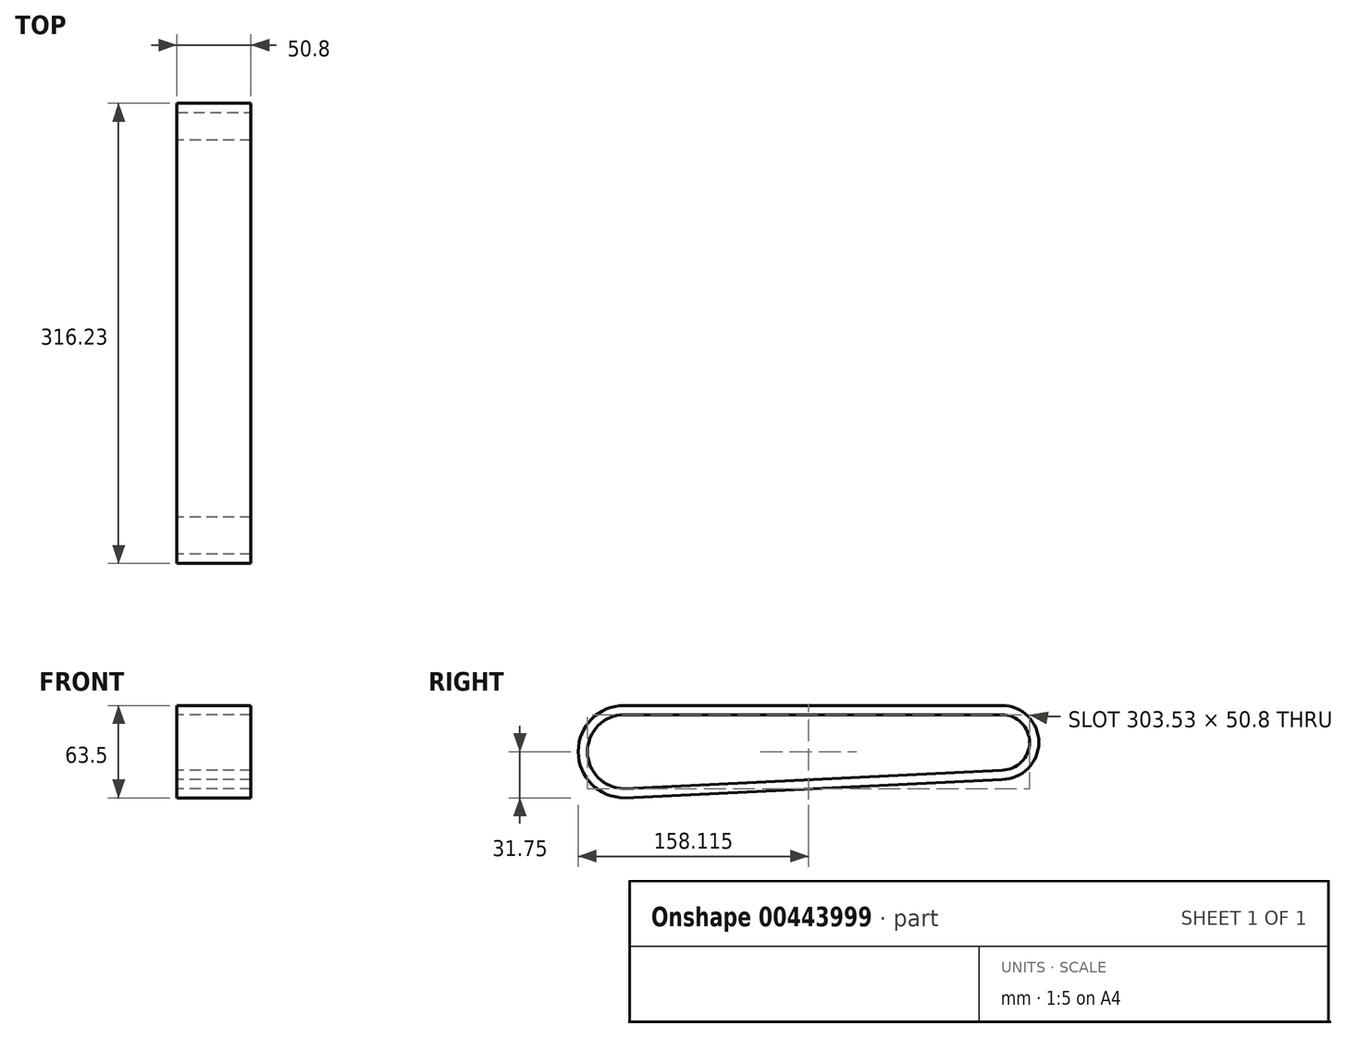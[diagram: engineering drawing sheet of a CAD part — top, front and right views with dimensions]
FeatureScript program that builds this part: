
annotation { "Feature Type Name" : "Feature", "Feature Type Description" : "" }
export const myFeature = defineFeature(function(context is Context, id is Id, definition is map)
    precondition{}
    {
        {
            var Q0;
            Q0=qCreatedBy(makeId("Front.planeOp"),FACE);
            var sketch = newSketch(context, id + "F0", { "sketchPlane" : qUnion([Q0])});
            skLineSegment(sketch, "E0.bottom", {"start": v(0, 0) * mm, "end": v(-50.8, 0) * mm});
            skLineSegment(sketch, "E0.top", {"start": v(0, 6.35) * mm, "end": v(-50.8, 6.35) * mm});
            skLineSegment(sketch, "E0.left", {"start": v(0, 0) * mm, "end": v(0, 6.35) * mm});
            skLineSegment(sketch, "E0.right", {"start": v(-50.8, 0) * mm, "end": v(-50.8, 6.35) * mm});
            skSolve(sketch);
        }
        {
            var Q0;
            Q0=makeQuery(id+"F0.imprint","IMPRINT",FACE,{"disambiguationData":[TD([[makeQuery(id+"F0.imprint","IMPRINT",EDGE,{"derivedFrom":sQuery(id+"F0.wireOp",EDGE,"E0.bottom")}),-1.0]])]});
            extrude(context, id + "F1", {"entities" : qUnion([Q0]), "depth" : 259.08 * mm});
        }
        {
            var Q0;
            Q0=makeQuery(id+"F1.opExtrude","CAP_FACE",FACE,{"disambiguationData":[OSD([sQuery(id+"F0.wireOp",EDGE,"E0.bottom"),sQuery(id+"F0.wireOp",EDGE,"E0.top"),sQuery(id+"F0.wireOp",EDGE,"E0.left"),sQuery(id+"F0.wireOp",EDGE,"E0.right")])],"isStart":false});
            var sketch = newSketch(context, id + "F2", { "sketchPlane" : qUnion([Q0])});
            skLineSegment(sketch, "E1.bottom", {"start": v(0, 0) * mm, "end": v(-50.8, 0) * mm});
            skLineSegment(sketch, "E1.top", {"start": v(0, 6.35) * mm, "end": v(-50.8, 6.35) * mm});
            skLineSegment(sketch, "E1.left", {"start": v(0, 0) * mm, "end": v(0, 6.35) * mm});
            skLineSegment(sketch, "E1.right", {"start": v(-50.8, 0) * mm, "end": v(-50.8, 6.35) * mm});
            skLineSegment(sketch, "E2", {"start": v(0, -25.4) * mm, "end": v(0, 0) * mm});
            skLineSegment(sketch, "E3", {"start": v(0, -25.4) * mm, "end": v(-50.8, -25.4) * mm});
            skSolve(sketch);
        }
        {
            var Q0;
            Q0=makeQuery(id+"F2.imprint","IMPRINT",FACE,{"disambiguationData":[TD([[makeQuery(id+"F2.imprint","IMPRINT",EDGE,{"derivedFrom":sQuery(id+"F2.wireOp",EDGE,"E1.bottom")}),-1.0]])]});
            var Q1;
            Q1=sQuery(id+"F2.wireOp",EDGE,"E3");
            revolve(context, id + "F3", {"operationType" : NewBodyOperationType.ADD, "entities" : qUnion([Q0]), "axis" : qUnion([Q1]), "revolveType" : RevolveType.ONE_DIRECTION, "oppositeDirection" : true, "angle" : 180 * degree});
        }
        {
            var Q0;
            Q0=makeQuery(id+"F1.opExtrude","CAP_FACE",FACE,{"disambiguationData":[OSD([sQuery(id+"F0.wireOp",EDGE,"E0.bottom"),sQuery(id+"F0.wireOp",EDGE,"E0.top"),sQuery(id+"F0.wireOp",EDGE,"E0.left"),sQuery(id+"F0.wireOp",EDGE,"E0.right")])],"isStart":true});
            var sketch = newSketch(context, id + "F4", { "sketchPlane" : qUnion([Q0])});
            skLineSegment(sketch, "E4.bottom", {"start": v(0, 0) * mm, "end": v(50.8, 0) * mm});
            skLineSegment(sketch, "E4.top", {"start": v(0, 6.35) * mm, "end": v(50.8, 6.35) * mm});
            skLineSegment(sketch, "E4.left", {"start": v(0, 0) * mm, "end": v(0, 6.35) * mm});
            skLineSegment(sketch, "E4.right", {"start": v(50.8, 0) * mm, "end": v(50.8, 6.35) * mm});
            skLineSegment(sketch, "E5", {"start": v(0, 0) * mm, "end": v(0, -19.05) * mm});
            skLineSegment(sketch, "E6", {"start": v(0, -19.05) * mm, "end": v(63.5, -19.05) * mm});
            skSolve(sketch);
        }
        {
            var Q0;
            Q0=makeQuery(id+"F4.imprint","IMPRINT",FACE,{"disambiguationData":[TD([[makeQuery(id+"F4.imprint","IMPRINT",EDGE,{"derivedFrom":sQuery(id+"F4.wireOp",EDGE,"E4.bottom")}),1.0]])]});
            var Q1;
            Q1=sQuery(id+"F4.wireOp",EDGE,"E6");
            revolve(context, id + "F5", {"operationType" : NewBodyOperationType.ADD, "entities" : qUnion([Q0]), "axis" : qUnion([Q1]), "revolveType" : RevolveType.ONE_DIRECTION, "angle" : 180 * degree});
        }
        {
            var Q0;
            Q0=makeQuery(id+"F5.boolean.opBoolean","MERGE",FACE,{"derivedFrom":[makeQuery(id+"F3.boolean.opBoolean","MERGE",FACE,{"derivedFrom":[makeQuery(id+"F1.opExtrude","SWEPT_FACE",FACE,{"disambiguationData":[OSD([sQuery(id+"F0.wireOp",EDGE,"E0.right")])]}),makeQuery(id+"F3.opRevolve","SWEPT_FACE",FACE,{"disambiguationData":[OSD([sQuery(id+"F2.wireOp",EDGE,"E1.right")])]})]}),makeQuery(id+"F5.opRevolve","SWEPT_FACE",FACE,{"disambiguationData":[OSD([sQuery(id+"F4.wireOp",EDGE,"E4.right")])]})]});
            var sketch = newSketch(context, id + "F6", { "sketchPlane" : qUnion([Q0])});
            skLineSegment(sketch, "E7", {"start": v(0, -38.1) * mm, "end": v(259.08, -50.8) * mm});
            skLineSegment(sketch, "E8", {"start": v(259.08, -50.8) * mm, "end": v(259.08, -57.15) * mm});
            skLineSegment(sketch, "E9", {"start": v(259.08, -57.15) * mm, "end": v(0, -44.45) * mm});
            skLineSegment(sketch, "E10", {"start": v(0, -44.45) * mm, "end": v(0, -38.1) * mm});
            skSolve(sketch);
        }
        {
            var Q0;
            Q0=makeQuery(id+"F6.imprint","IMPRINT",FACE,{"disambiguationData":[TD([[makeQuery(id+"F6.imprint","IMPRINT",EDGE,{"derivedFrom":sQuery(id+"F6.wireOp",EDGE,"E7")}),-1.0]])]});
            extrude(context, id + "F7", {"entities" : qUnion([Q0]), "operationType" : NewBodyOperationType.ADD, "oppositeDirection" : true, "depth" : 50.8 * mm});
        }
    });
